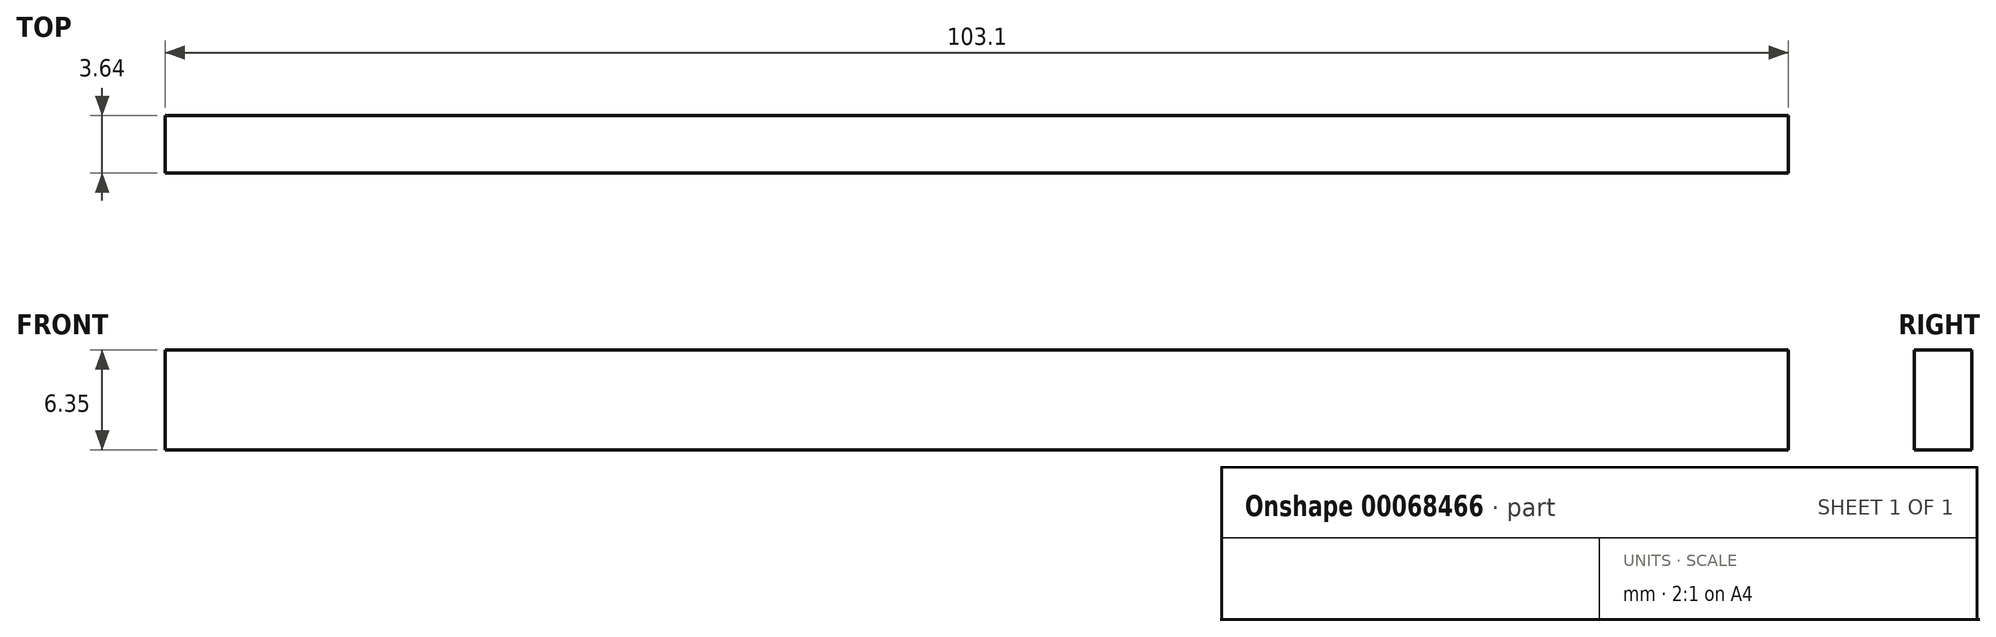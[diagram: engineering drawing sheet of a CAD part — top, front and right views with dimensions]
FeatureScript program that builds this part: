
annotation { "Feature Type Name" : "Feature", "Feature Type Description" : "" }
export const myFeature = defineFeature(function(context is Context, id is Id, definition is map)
    precondition{}
    {
        {
            var Q0;
            Q0=qCreatedBy(makeId("Top.planeOp"),FACE);
            var sketch = newSketch(context, id + "F0", { "sketchPlane" : qUnion([Q0])});
            skLineSegment(sketch, "E0.rect.bottom", {"start": v(51.55, -1.83) * mm, "end": v(-51.55, -1.83) * mm});
            skLineSegment(sketch, "E0.rect.top", {"start": v(51.55, 1.82) * mm, "end": v(-51.55, 1.82) * mm});
            skLineSegment(sketch, "E0.rect.left", {"start": v(51.55, -1.83) * mm, "end": v(51.55, 1.83) * mm});
            skLineSegment(sketch, "E0.rect.right", {"start": v(-51.55, -1.83) * mm, "end": v(-51.55, 1.82) * mm});
            skPoint(sketch, "E0.rect.middle", {"position": v(0, 0) * mm});
            skSolve(sketch);
        }
        {
            var Q0;
            Q0 = qSketchRegion(id + "F0", true);
            extrude(context, id + "F1", {"entities" : qUnion([Q0]), "depth" : 6.35 * mm});
        }
    });
